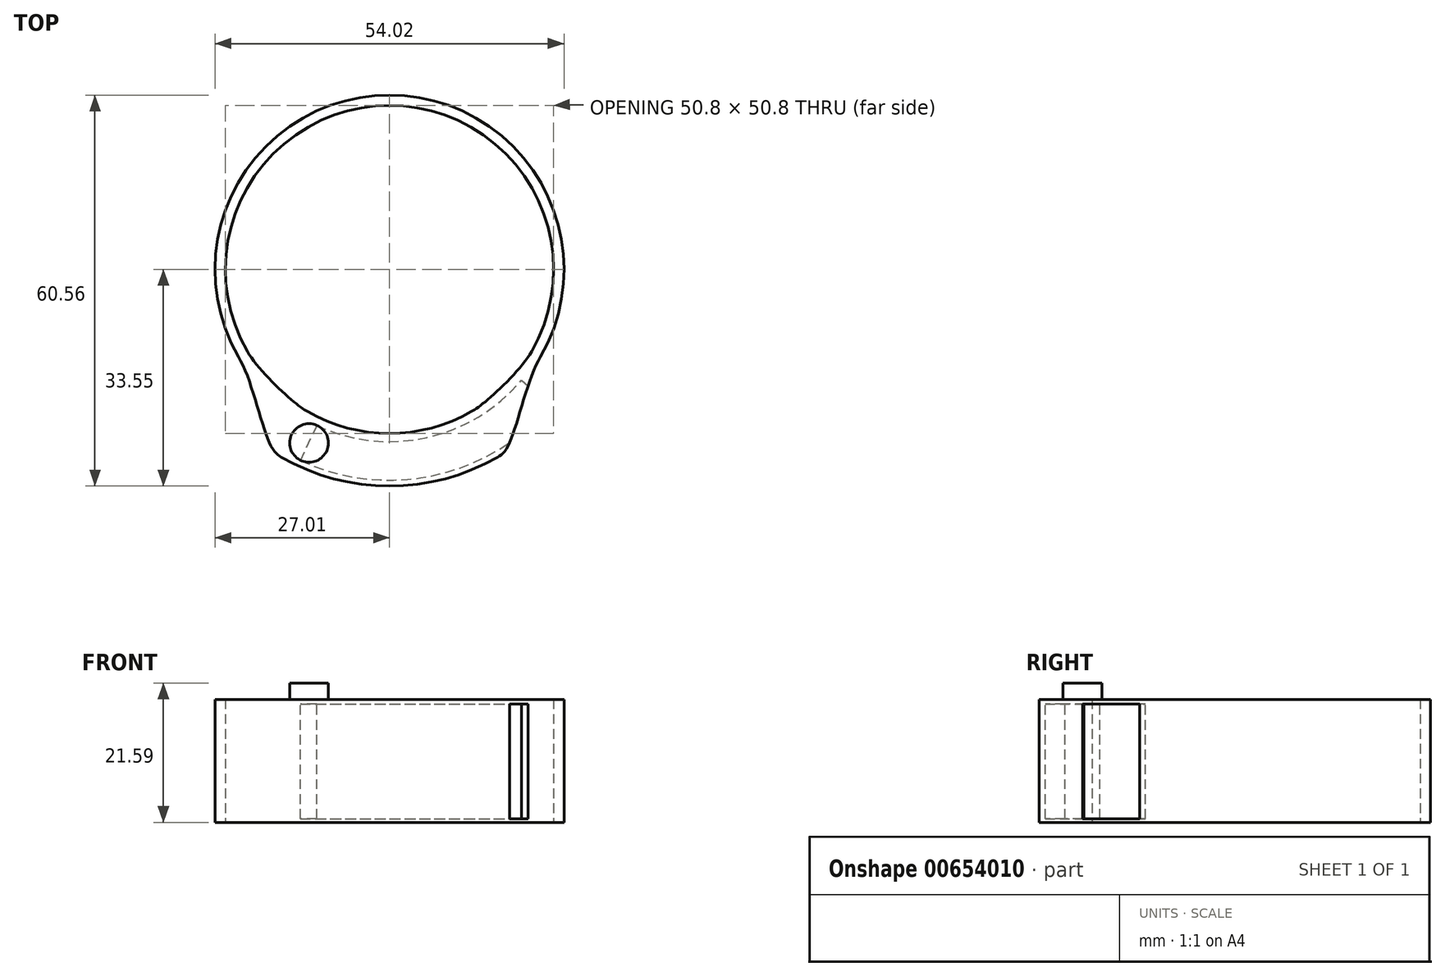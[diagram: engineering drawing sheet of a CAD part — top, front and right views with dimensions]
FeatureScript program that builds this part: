
annotation { "Feature Type Name" : "Feature", "Feature Type Description" : "" }
export const myFeature = defineFeature(function(context is Context, id is Id, definition is map)
    precondition{}
    {
        {
            var Q0;
            Q0=qCreatedBy(makeId("Front.planeOp"),FACE);
            var sketch = newSketch(context, id + "F0", { "sketchPlane" : qUnion([Q0])});
            skLineSegment(sketch, "E0.bottom", {"start": v(25.4, 0) * mm, "end": v(27, 0) * mm});
            skLineSegment(sketch, "E0.top", {"start": v(25.4, 19.05) * mm, "end": v(27, 19.05) * mm});
            skLineSegment(sketch, "E0.left", {"start": v(25.4, 0) * mm, "end": v(25.4, 19.05) * mm});
            skLineSegment(sketch, "E0.right", {"start": v(27, 0) * mm, "end": v(27, 19.05) * mm});
            skSolve(sketch);
        }
        {
            var Q0;
            Q0=qCreatedBy(makeId("Front.planeOp"),FACE);
            var sketch = newSketch(context, id + "F1", { "sketchPlane" : qUnion([Q0])});
            skLineSegment(sketch, "E1", {"start": v(0, 0) * mm, "end": v(0, 61.6) * mm});
            skSolve(sketch);
        }
        {
            var Q0;
            Q0=qSketchRegion(id+"F0",true);
            var Q1;
            Q1=sQuery(id+"F1.wireOp",EDGE,"E1");
            revolve(context, id + "F2", {"entities" : qUnion([Q0]), "axis" : qUnion([Q1]), "revolveType" : RevolveType.TWO_DIRECTIONS, "angle" : 210 * degree, "angleBack" : 330 * degree});
        }
        {
            var Q0;
            Q0=qCreatedBy(makeId("Right.planeOp"),FACE);
            var sketch = newSketch(context, id + "F3", { "sketchPlane" : qUnion([Q0])});
            skLineSegment(sketch, "E2.bottom", {"start": v(-25.4, 0) * mm, "end": v(-33.55, 0) * mm});
            skLineSegment(sketch, "E2.top", {"start": v(-25.4, 19.05) * mm, "end": v(-33.55, 19.05) * mm});
            skLineSegment(sketch, "E2.left", {"start": v(-25.4, 0) * mm, "end": v(-25.4, 19.05) * mm});
            skLineSegment(sketch, "E2.right", {"start": v(-33.55, 0) * mm, "end": v(-33.55, 19.05) * mm});
            skSolve(sketch);
        }
        {
            var Q0;
            Q0=qSketchRegion(id+"F3",true);
            var Q1;
            Q1=sQuery(id+"F1.wireOp",EDGE,"E1");
            revolve(context, id + "F4", {"entities" : qUnion([Q0]), "axis" : qUnion([Q1]), "revolveType" : RevolveType.TWO_DIRECTIONS, "angle" : 30 * degree, "angleBack" : 330 * degree});
        }
        {
            var Q0;
            Q0=makeQuery(id+"F4.opRevolve","CAP_FACE",FACE,{"disambiguationData":[OSD([sQuery(id+"F3.wireOp",EDGE,"E2.bottom"),sQuery(id+"F3.wireOp",EDGE,"E2.top"),sQuery(id+"F3.wireOp",EDGE,"E2.left"),sQuery(id+"F3.wireOp",EDGE,"E2.right")])],"isStart":true});
            var Q1;
            Q1=makeQuery(id+"F2.opRevolve","CAP_FACE",FACE,{"disambiguationData":[OSD([sQuery(id+"F0.wireOp",EDGE,"E0.bottom"),sQuery(id+"F0.wireOp",EDGE,"E0.top"),sQuery(id+"F0.wireOp",EDGE,"E0.left"),sQuery(id+"F0.wireOp",EDGE,"E0.right")])],"isStart":false});
            loft(context, id + "F5", {"operationType" : NewBodyOperationType.ADD, "startCondition" : LoftEndDerivativeType.MATCH_CURVATURE, "startMagnitude" : .5, "endCondition" : LoftEndDerivativeType.MATCH_TANGENT, "endMagnitude" : 1, "sheetProfilesArray" : [{ "sheetProfileEntities" : qUnion([Q0]) }, { "sheetProfileEntities" : qUnion([Q1]) }]});
        }
        {
            var Q1;
            Q1=makeQuery(id+"F4.opRevolve","CAP_FACE",FACE,{"disambiguationData":[OSD([sQuery(id+"F3.wireOp",EDGE,"E2.bottom"),sQuery(id+"F3.wireOp",EDGE,"E2.top"),sQuery(id+"F3.wireOp",EDGE,"E2.left"),sQuery(id+"F3.wireOp",EDGE,"E2.right")])],"isStart":false});
            var Q2;
            Q2=makeQuery(id+"F2.opRevolve","CAP_FACE",FACE,{"disambiguationData":[OSD([sQuery(id+"F0.wireOp",EDGE,"E0.bottom"),sQuery(id+"F0.wireOp",EDGE,"E0.top"),sQuery(id+"F0.wireOp",EDGE,"E0.left"),sQuery(id+"F0.wireOp",EDGE,"E0.right")])],"isStart":true});
            loft(context, id + "F6", {"operationType" : NewBodyOperationType.ADD, "startCondition" : LoftEndDerivativeType.MATCH_CURVATURE, "startMagnitude" : .5, "endCondition" : LoftEndDerivativeType.MATCH_TANGENT, "endMagnitude" : 1, "sheetProfilesArray" : [{ "sheetProfileEntities" : qUnion([Q1]) }, { "sheetProfileEntities" : qUnion([Q2]) }]});
        }
        {
            var Q0;
            Q0=qCreatedBy(makeId("Right.planeOp"),FACE);
            var sketch = newSketch(context, id + "F7", { "sketchPlane" : qUnion([Q0])});
            skLineSegment(sketch, "E3.bottom", {"start": v(-26.67, 0.56) * mm, "end": v(-32.64, 0.56) * mm});
            skLineSegment(sketch, "E3.top", {"start": v(-26.67, 18.34) * mm, "end": v(-32.64, 18.34) * mm});
            skLineSegment(sketch, "E3.left", {"start": v(-26.67, 0.56) * mm, "end": v(-26.67, 18.34) * mm});
            skLineSegment(sketch, "E3.right", {"start": v(-32.64, 0.56) * mm, "end": v(-32.64, 18.34) * mm});
            skSolve(sketch);
        }
        {
            var Q0;
            Q0=qSketchRegion(id+"F7",true);
            var Q1;
            Q1=sQuery(id+"F1.wireOp",EDGE,"E1");
            revolve(context, id + "F8", {"operationType" : NewBodyOperationType.REMOVE, "entities" : qUnion([Q0]), "axis" : qUnion([Q1]), "revolveType" : RevolveType.TWO_DIRECTIONS, "oppositeDirection" : true, "angle" : 25 * degree, "angleBack" : 310 * degree});
        }
        {
            var Q0;
            {var subQ0=sQuery(id+"F3.wireOp",EDGE,"E2.right");var subQ1=sQuery(id+"F3.wireOp",EDGE,"E2.left");var subQ2=sQuery(id+"F3.wireOp",EDGE,"E2.top");var subQ3=sQuery(id+"F0.wireOp",EDGE,"E0.right");var subQ4=sQuery(id+"F0.wireOp",EDGE,"E0.left");var subQ5=sQuery(id+"F0.wireOp",EDGE,"E0.top");Q0=makeQuery(id+"F6.boolean.opBoolean","MERGE",FACE,{"derivedFrom":[makeQuery(id+"F5.boolean.opBoolean","MERGE",FACE,{"derivedFrom":[makeQuery(id+"F2.opRevolve","SWEPT_FACE",FACE,{"disambiguationData":[OSD([subQ5])]}),makeQuery(id+"F4.opRevolve","SWEPT_FACE",FACE,{"disambiguationData":[OSD([subQ2])]}),makeQuery(id+"F5.opLoft","SWEPT_FACE",FACE,{"disambiguationData":[OSD([subQ5,subQ4,subQ3,subQ2,subQ1,subQ0])]})]}),makeQuery(id+"F6.opLoft","SWEPT_FACE",FACE,{"disambiguationData":[OSD([subQ5,subQ4,subQ3,subQ2,subQ1,subQ0])]})]});}
            var sketch = newSketch(context, id + "F9", { "sketchPlane" : qUnion([Q0])});
            skCircle(sketch, "E4", {"center": v(-12.45, -26.87) * mm, "radius": 3 * mm});
            skSolve(sketch);
        }
        {
            var Q0;
            Q0=qSketchRegion(id+"F9",true);
            extrude(context, id + "F10", {"entities" : qUnion([Q0]), "operationType" : NewBodyOperationType.ADD, "depth" : 2.54 * mm, "offsetDistance" : 25.4 * mm});
        }
    });
